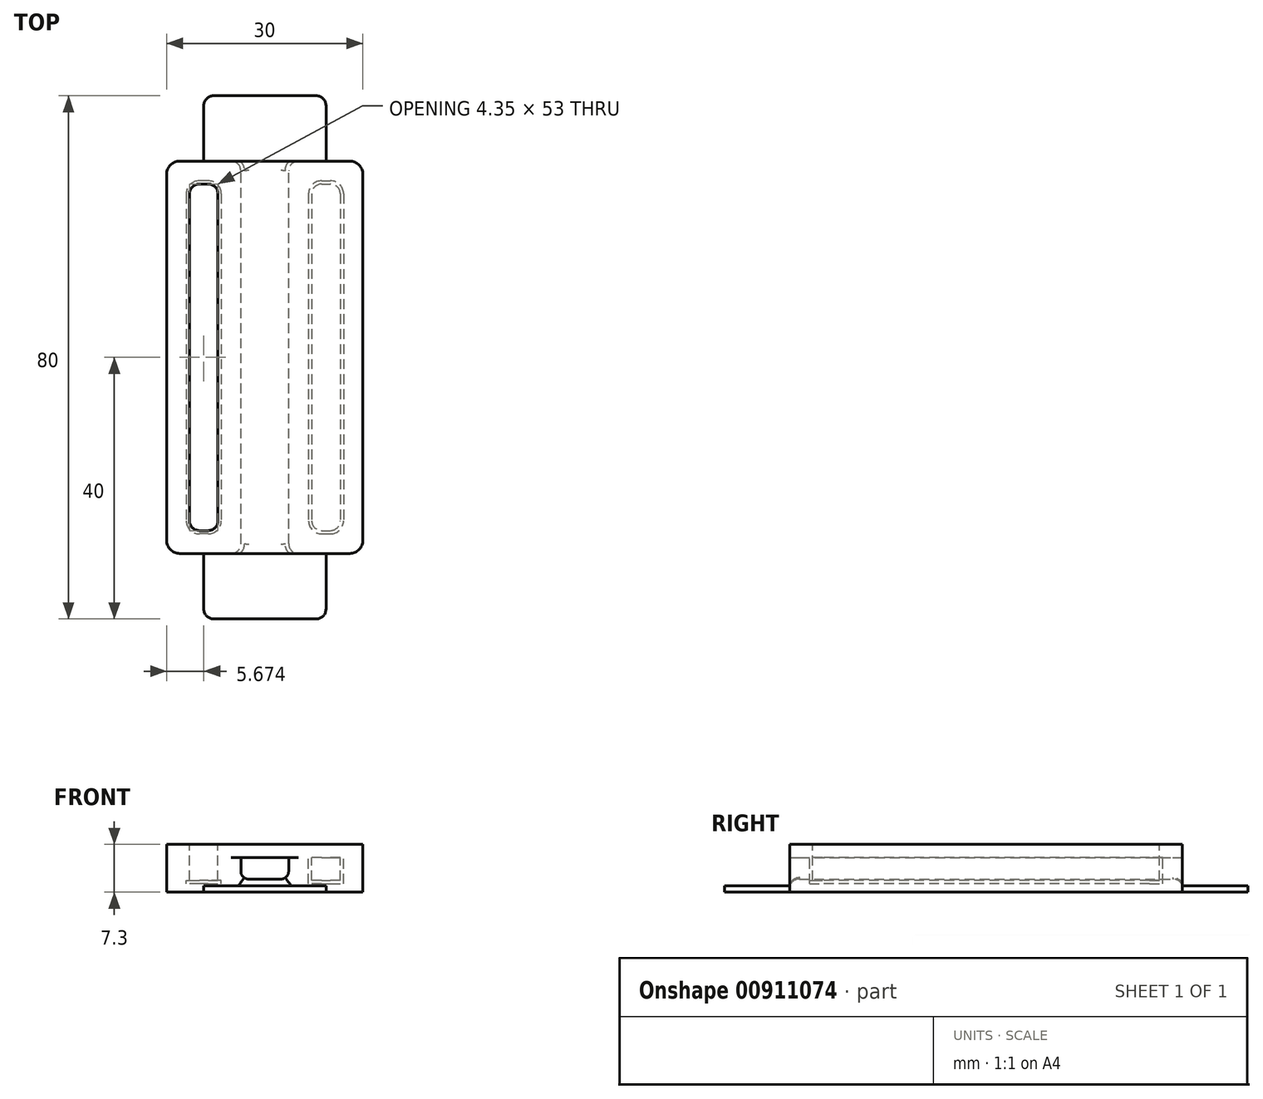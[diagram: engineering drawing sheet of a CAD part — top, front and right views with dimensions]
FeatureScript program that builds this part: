
annotation { "Feature Type Name" : "Feature", "Feature Type Description" : "" }
export const myFeature = defineFeature(function(context is Context, id is Id, definition is map)
    precondition{}
    {
        {
            var Q0;
            Q0=qCreatedBy(makeId("Front.planeOp"),FACE);
            var sketch = newSketch(context, id + "F0", { "sketchPlane" : qUnion([Q0])});
            skLineSegment(sketch, "E0", {"start": v(0, 0) * mm, "end": v(14.98, 0) * mm});
            skLineSegment(sketch, "E1", {"start": v(14.98, 0) * mm, "end": v(14.98, 5.3) * mm});
            skLineSegment(sketch, "E2", {"start": v(14.98, 5.3) * mm, "end": v(3.63, 5.3) * mm});
            skLineSegment(sketch, "E3", {"start": v(3.63, 5.3) * mm, "end": v(3.63, 3.2) * mm});
            skLineSegment(sketch, "E4", {"start": v(2.43, 2) * mm, "end": v(-0.25, 2) * mm});
            skLineSegment(sketch, "E5.MirrorCS", {"start": v(-15.02, 5.3) * mm, "end": v(-3.67, 5.3) * mm});
            skLineSegment(sketch, "E6.MirrorCS", {"start": v(-3.67, 5.3) * mm, "end": v(-3.67, 3.2) * mm});
            skLineSegment(sketch, "E7.MirrorCS", {"start": v(-2.47, 2) * mm, "end": v(0.2, 2) * mm});
            skLineSegment(sketch, "E8.MirrorCS", {"start": v(-15.02, 0) * mm, "end": v(-15.02, 5.3) * mm});
            skLineSegment(sketch, "E9.MirrorCS", {"start": v(0, 0) * mm, "end": v(-15.02, 0) * mm});
            skPoint(sketch, "E10.visualSharp", {"position": v(-3.67, 2) * mm});
            skArc(sketch, "E10.filletArc", {"start": v(-3.67, 3.2) * mm, "mid": v(-3.32, 2.35) * mm, "end": v(-2.47, 2) * mm});
            skPoint(sketch, "E11.visualSharp", {"position": v(3.63, 2) * mm});
            skArc(sketch, "E11.filletArc", {"start": v(2.43, 2) * mm, "mid": v(3.28, 2.35) * mm, "end": v(3.63, 3.2) * mm});
            skSolve(sketch);
        }
        {
            var Q0;
            Q0 = qSketchRegion(id + "F0", true);
            extrude(context, id + "F1", {"entities" : qUnion([Q0]), "depth" : 60 * mm, "offsetDistance" : 25 * mm});
        }
        {
            var Q0;
            Q0=makeQuery(id+"F1.opExtrude","SWEPT_FACE",FACE,{"disambiguationData":[OSD([sQuery(id+"F0.wireOp",EDGE,"E5.MirrorCS")])]});
            var sketch = newSketch(context, id + "F2", { "sketchPlane" : qUnion([Q0])});
            skLineSegment(sketch, "E12.bottom", {"start": v(-6.67, -3) * mm, "end": v(-12.02, -3) * mm});
            skLineSegment(sketch, "E12.top", {"start": v(-6.67, -57) * mm, "end": v(-12.02, -57) * mm});
            skLineSegment(sketch, "E12.left", {"start": v(-6.67, -3) * mm, "end": v(-6.67, -57) * mm});
            skLineSegment(sketch, "E12.right", {"start": v(-12.02, -3) * mm, "end": v(-12.02, -57) * mm});
            skLineSegment(sketch, "E13.MirrorCS", {"start": v(6.67, -3) * mm, "end": v(12.02, -3) * mm});
            skLineSegment(sketch, "E14.MirrorCS", {"start": v(12.02, -3) * mm, "end": v(12.02, -57) * mm});
            skLineSegment(sketch, "E15.MirrorCS", {"start": v(6.67, -57) * mm, "end": v(12.02, -57) * mm});
            skLineSegment(sketch, "E16.MirrorCS", {"start": v(6.67, -3) * mm, "end": v(6.67, -57) * mm});
            skSolve(sketch);
        }
        {
            var Q0;
            Q0 = qSketchRegion(id + "F2", true);
            extrude(context, id + "F3", {"entities" : qUnion([Q0]), "operationType" : NewBodyOperationType.REMOVE, "oppositeDirection" : true, "depth" : 4 * mm, "offsetDistance" : 25 * mm});
        }
        {
            var Q0;
            Q0=makeQuery(id+"F3.boolean.opBoolean","COPY",EDGE,{"derivedFrom":makeQuery(id+"F3.opExtrude","SWEPT_EDGE",EDGE,{"disambiguationData":[OSD([sQuery(id+"F2.wireOp",EDGE,"E12.bottom"),sQuery(id+"F2.wireOp",EDGE,"E12.left")])]})});
            var Q1;
            Q1=makeQuery(id+"F3.boolean.opBoolean","COPY",EDGE,{"derivedFrom":makeQuery(id+"F3.opExtrude","SWEPT_EDGE",EDGE,{"disambiguationData":[OSD([sQuery(id+"F2.wireOp",EDGE,"E12.bottom"),sQuery(id+"F2.wireOp",EDGE,"E12.right")])]})});
            var Q2;
            Q2=makeQuery(id+"F3.boolean.opBoolean","COPY",EDGE,{"derivedFrom":makeQuery(id+"F3.opExtrude","SWEPT_EDGE",EDGE,{"disambiguationData":[OSD([sQuery(id+"F2.wireOp",EDGE,"E12.top"),sQuery(id+"F2.wireOp",EDGE,"E12.right")])]})});
            var Q3;
            Q3=makeQuery(id+"F3.boolean.opBoolean","COPY",EDGE,{"derivedFrom":makeQuery(id+"F3.opExtrude","SWEPT_EDGE",EDGE,{"disambiguationData":[OSD([sQuery(id+"F2.wireOp",EDGE,"E12.top"),sQuery(id+"F2.wireOp",EDGE,"E12.left")])]})});
            var Q4;
            Q4=makeQuery(id+"F3.boolean.opBoolean","COPY",EDGE,{"derivedFrom":makeQuery(id+"F3.opExtrude","SWEPT_EDGE",EDGE,{"disambiguationData":[OSD([sQuery(id+"F2.wireOp",EDGE,"E13.MirrorCS"),sQuery(id+"F2.wireOp",EDGE,"E16.MirrorCS")])]})});
            var Q5;
            Q5=makeQuery(id+"F3.boolean.opBoolean","COPY",EDGE,{"derivedFrom":makeQuery(id+"F3.opExtrude","SWEPT_EDGE",EDGE,{"disambiguationData":[OSD([sQuery(id+"F2.wireOp",EDGE,"E13.MirrorCS"),sQuery(id+"F2.wireOp",EDGE,"E14.MirrorCS")])]})});
            var Q6;
            Q6=makeQuery(id+"F3.boolean.opBoolean","COPY",EDGE,{"derivedFrom":makeQuery(id+"F3.opExtrude","SWEPT_EDGE",EDGE,{"disambiguationData":[OSD([sQuery(id+"F2.wireOp",EDGE,"E15.MirrorCS"),sQuery(id+"F2.wireOp",EDGE,"E16.MirrorCS")])]})});
            var Q7;
            Q7=makeQuery(id+"F3.boolean.opBoolean","COPY",EDGE,{"derivedFrom":makeQuery(id+"F3.opExtrude","SWEPT_EDGE",EDGE,{"disambiguationData":[OSD([sQuery(id+"F2.wireOp",EDGE,"E14.MirrorCS"),sQuery(id+"F2.wireOp",EDGE,"E15.MirrorCS")])]})});
            var Q8;
            Q8=makeQuery(id+"F1.opExtrude","CAP_EDGE",EDGE,{"disambiguationData":[OSD([sQuery(id+"F0.wireOp",EDGE,"E8.MirrorCS")])],"isStart":true});
            var Q9;
            Q9=makeQuery(id+"F1.opExtrude","CAP_EDGE",EDGE,{"disambiguationData":[OSD([sQuery(id+"F0.wireOp",EDGE,"E1")])],"isStart":true});
            var Q10;
            Q10=makeQuery(id+"F1.opExtrude","CAP_EDGE",EDGE,{"disambiguationData":[OSD([sQuery(id+"F0.wireOp",EDGE,"E1")])],"isStart":false});
            var Q11;
            Q11=makeQuery(id+"F1.opExtrude","CAP_EDGE",EDGE,{"disambiguationData":[OSD([sQuery(id+"F0.wireOp",EDGE,"E8.MirrorCS")])],"isStart":false});
            fillet(context, id + "F4", {"entities" : qUnion([Q0, Q1, Q2, Q3, Q4, Q5, Q6, Q7, Q8, Q9, Q10, Q11]), "radius" : 2 * mm, "tangentPropagation" : true, "allowEdgeOverflow" : false});
        }
        {
            var Q0;
            Q0=qCreatedBy(makeId("Top.planeOp"),FACE);
            var sketch = newSketch(context, id + "F5", { "sketchPlane" : qUnion([Q0])});
            skLineSegment(sketch, "E17.bottom", {"start": v(9.35, 0) * mm, "end": v(-9.35, 0) * mm});
            skLineSegment(sketch, "E17.top", {"start": v(9.35, 10) * mm, "end": v(-9.35, 10) * mm});
            skLineSegment(sketch, "E17.left", {"start": v(9.35, 0) * mm, "end": v(9.35, 10) * mm});
            skLineSegment(sketch, "E17.right", {"start": v(-9.35, 0) * mm, "end": v(-9.35, 10) * mm});
            skPoint(sketch, "E18.0", {"position": v(9.35, -3) * mm});
            skPoint(sketch, "E19.0", {"position": v(-9.35, -3) * mm});
            skPoint(sketch, "E20.0", {"position": v(6.67, -30) * mm});
            skPoint(sketch, "E20.1", {"position": v(-6.67, -30) * mm});
            skLineSegment(sketch, "E21", {"start": v(6.67, -30) * mm, "end": v(-6.67, -30) * mm});
            skLineSegment(sketch, "E22.MirrorCS", {"start": v(9.35, -60) * mm, "end": v(9.35, -70) * mm});
            skLineSegment(sketch, "E23.MirrorCS", {"start": v(9.35, -70) * mm, "end": v(-9.35, -70) * mm});
            skLineSegment(sketch, "E24.MirrorCS", {"start": v(-9.35, -60) * mm, "end": v(-9.35, -70) * mm});
            skLineSegment(sketch, "E25.MirrorCS", {"start": v(9.35, -60) * mm, "end": v(-9.35, -60) * mm});
            skSolve(sketch);
        }
        {
            var Q0;
            Q0=makeQuery(id+"F5.imprint","IMPRINT",FACE,{"disambiguationData":[TD([[makeQuery(id+"F5.imprint","IMPRINT",EDGE,{"derivedFrom":sQuery(id+"F5.wireOp",EDGE,"E17.bottom")}),-1.0]])]});
            var Q1;
            Q1=makeQuery(id+"F5.imprint","IMPRINT",FACE,{"disambiguationData":[TD([[makeQuery(id+"F5.imprint","IMPRINT",EDGE,{"derivedFrom":sQuery(id+"F5.wireOp",EDGE,"E22.MirrorCS")}),-1.0]])]});
            extrude(context, id + "F6", {"entities" : qUnion([Q0, Q1]), "operationType" : NewBodyOperationType.ADD, "depth" : 1 * mm, "offsetDistance" : 25 * mm});
        }
        {
            var Q0;
            Q0=makeQuery(id+"F6.opExtrude","SWEPT_EDGE",EDGE,{"disambiguationData":[OSD([sQuery(id+"F5.wireOp",EDGE,"E23.MirrorCS"),sQuery(id+"F5.wireOp",EDGE,"E24.MirrorCS")])]});
            var Q1;
            Q1=makeQuery(id+"F6.opExtrude","SWEPT_EDGE",EDGE,{"disambiguationData":[OSD([sQuery(id+"F5.wireOp",EDGE,"E22.MirrorCS"),sQuery(id+"F5.wireOp",EDGE,"E23.MirrorCS")])]});
            var Q2;
            Q2=makeQuery(id+"F1.opExtrude","CAP_EDGE",EDGE,{"disambiguationData":[OSD([sQuery(id+"F0.wireOp",EDGE,"E4"),sQuery(id+"F0.wireOp",EDGE,"E7.MirrorCS")])],"isStart":false});
            var Q3;
            Q3=makeQuery(id+"F1.opExtrude","CAP_EDGE",EDGE,{"disambiguationData":[OSD([sQuery(id+"F0.wireOp",EDGE,"E4"),sQuery(id+"F0.wireOp",EDGE,"E7.MirrorCS")])],"isStart":true});
            var Q4;
            Q4=makeQuery(id+"F6.opExtrude","SWEPT_EDGE",EDGE,{"disambiguationData":[OSD([sQuery(id+"F5.wireOp",EDGE,"E17.top"),sQuery(id+"F5.wireOp",EDGE,"E17.right")])]});
            var Q5;
            Q5=makeQuery(id+"F6.opExtrude","SWEPT_EDGE",EDGE,{"disambiguationData":[OSD([sQuery(id+"F5.wireOp",EDGE,"E17.top"),sQuery(id+"F5.wireOp",EDGE,"E17.left")])]});
            fillet(context, id + "F7", {"entities" : qUnion([Q0, Q1, Q2, Q3, Q4, Q5]), "radius" : 1.5 * mm, "tangentPropagation" : true, "allowEdgeOverflow" : false});
        }
        {
            var Q0;
            Q0=makeQuery(id+"F1.opExtrude","SWEPT_FACE",FACE,{"disambiguationData":[OSD([sQuery(id+"F0.wireOp",EDGE,"E5.MirrorCS")])]});
            var sketch = newSketch(context, id + "F8", { "sketchPlane" : qUnion([Q0])});
            skLineSegment(sketch, "E26.0", {"start": v(-12.02, -5) * mm, "end": v(-12.02, -55) * mm});
            skArc(sketch, "E26.1", {"start": v(-10.02, -57) * mm, "mid": v(-11.44, -56.41) * mm, "end": v(-12.02, -55) * mm});
            skLineSegment(sketch, "E26.2", {"start": v(-8.67, -57) * mm, "end": v(-10.02, -57) * mm});
            skArc(sketch, "E26.3", {"start": v(-6.67, -55) * mm, "mid": v(-7.26, -56.41) * mm, "end": v(-8.67, -57) * mm});
            skLineSegment(sketch, "E26.4", {"start": v(-6.67, -5) * mm, "end": v(-6.67, -55) * mm});
            skArc(sketch, "E26.5", {"start": v(-8.67, -3) * mm, "mid": v(-7.26, -3.59) * mm, "end": v(-6.67, -5) * mm});
            skLineSegment(sketch, "E26.6", {"start": v(-8.67, -3) * mm, "end": v(-10.02, -3) * mm});
            skArc(sketch, "E26.7", {"start": v(-12.02, -5) * mm, "mid": v(-11.44, -3.59) * mm, "end": v(-10.02, -3) * mm});
            skArc(sketch, "E27.0", {"start": v(-8.67, -3.5) * mm, "mid": v(-7.61, -3.94) * mm, "end": v(-7.17, -5) * mm});
            skLineSegment(sketch, "E27.1", {"start": v(-8.67, -3.5) * mm, "end": v(-10.02, -3.5) * mm});
            skLineSegment(sketch, "E27.2", {"start": v(-7.17, -5) * mm, "end": v(-7.17, -55) * mm});
            skArc(sketch, "E27.3", {"start": v(-11.52, -5) * mm, "mid": v(-11.08, -3.94) * mm, "end": v(-10.02, -3.5) * mm});
            skArc(sketch, "E27.4", {"start": v(-7.17, -55) * mm, "mid": v(-7.61, -56.06) * mm, "end": v(-8.67, -56.5) * mm});
            skLineSegment(sketch, "E27.5", {"start": v(-8.67, -56.5) * mm, "end": v(-10.02, -56.5) * mm});
            skArc(sketch, "E27.6", {"start": v(-10.02, -56.5) * mm, "mid": v(-11.08, -56.06) * mm, "end": v(-11.52, -55) * mm});
            skLineSegment(sketch, "E27.7", {"start": v(-11.52, -5) * mm, "end": v(-11.52, -55) * mm});
            skLineSegment(sketch, "E28.MirrorCS", {"start": v(11.52, -5) * mm, "end": v(11.52, -55) * mm});
            skArc(sketch, "E29.MirrorCS", {"start": v(10.02, -56.5) * mm, "mid": v(11.08, -56.06) * mm, "end": v(11.52, -55) * mm});
            skLineSegment(sketch, "E30.MirrorCS", {"start": v(8.67, -56.5) * mm, "end": v(10.02, -56.5) * mm});
            skArc(sketch, "E31.MirrorCS", {"start": v(7.17, -55) * mm, "mid": v(7.61, -56.06) * mm, "end": v(8.67, -56.5) * mm});
            skLineSegment(sketch, "E32.MirrorCS", {"start": v(7.17, -5) * mm, "end": v(7.17, -55) * mm});
            skArc(sketch, "E33.MirrorCS", {"start": v(8.67, -3.5) * mm, "mid": v(7.61, -3.94) * mm, "end": v(7.17, -5) * mm});
            skLineSegment(sketch, "E34.MirrorCS", {"start": v(8.67, -3.5) * mm, "end": v(10.02, -3.5) * mm});
            skArc(sketch, "E35.MirrorCS", {"start": v(11.52, -5) * mm, "mid": v(11.08, -3.94) * mm, "end": v(10.02, -3.5) * mm});
            skLineSegment(sketch, "E36.0", {"start": v(-15.02, -58) * mm, "end": v(-15.02, -2) * mm});
            skArc(sketch, "E36.1", {"start": v(-15.02, -58) * mm, "mid": v(-14.44, -59.41) * mm, "end": v(-13.02, -60) * mm});
            skLineSegment(sketch, "E36.2", {"start": v(-13.02, -60) * mm, "end": v(-5.17, -60) * mm});
            skLineSegment(sketch, "E36.3", {"start": v(12.98, -60) * mm, "end": v(5.13, -60) * mm});
            skArc(sketch, "E36.4", {"start": v(12.98, -60) * mm, "mid": v(14.4, -59.41) * mm, "end": v(14.98, -58) * mm});
            skLineSegment(sketch, "E36.5", {"start": v(14.98, -58) * mm, "end": v(14.98, -2) * mm});
            skArc(sketch, "E36.6", {"start": v(14.98, -2) * mm, "mid": v(14.4, -0.59) * mm, "end": v(12.98, 0) * mm});
            skLineSegment(sketch, "E36.7", {"start": v(12.98, 0) * mm, "end": v(5.13, 0) * mm});
            skLineSegment(sketch, "E36.8", {"start": v(-13.02, 0) * mm, "end": v(-5.17, 0) * mm});
            skArc(sketch, "E36.9", {"start": v(-13.02, 0) * mm, "mid": v(-14.44, -0.59) * mm, "end": v(-15.02, -2) * mm});
            skLineSegment(sketch, "E37", {"start": v(5.13, -60) * mm, "end": v(-5.17, -60) * mm});
            skLineSegment(sketch, "E38", {"start": v(5.13, 0) * mm, "end": v(-5.17, 0) * mm});
            skSolve(sketch);
        }
        {
            var Q0;
            Q0=makeQuery(id+"F8.imprint","IMPRINT",FACE,{"disambiguationData":[TD([[makeQuery(id+"F8.imprint","IMPRINT",EDGE,{"derivedFrom":sQuery(id+"F8.wireOp",EDGE,"E28.MirrorCS")}),-1.0]])]});
            var Q1;
            Q1=makeQuery(id+"F8.imprint","IMPRINT",FACE,{"disambiguationData":[TD([[makeQuery(id+"F8.imprint","IMPRINT",EDGE,{"derivedFrom":sQuery(id+"F8.wireOp",EDGE,"E27.0")}),-1.0]])]});
            extrude(context, id + "F9", {"entities" : qUnion([Q0, Q1]), "oppositeDirection" : true, "depth" : 3.5 * mm, "offsetDistance" : 25 * mm, "hasSecondDirection" : true, "secondDirectionOppositeDirection" : false, "secondDirectionDepth" : 2 * mm});
        }
        {
            var Q0;
            Q0=makeQuery(id+"F8.imprint","IMPRINT",FACE,{"disambiguationData":[TD([[makeQuery(id+"F8.imprint","IMPRINT",EDGE,{"derivedFrom":sQuery(id+"F8.wireOp",EDGE,"E26.0")}),-1.0]])]});
            var Q1;
            Q1=makeQuery(id+"F8.imprint","IMPRINT",FACE,{"disambiguationData":[TD([[makeQuery(id+"F8.imprint","IMPRINT",EDGE,{"derivedFrom":sQuery(id+"F8.wireOp",EDGE,"E28.MirrorCS")}),1.0]])]});
            var Q2;
            Q2=makeQuery(id+"F8.imprint","IMPRINT",FACE,{"disambiguationData":[TD([[makeQuery(id+"F8.imprint","IMPRINT",EDGE,{"derivedFrom":sQuery(id+"F8.wireOp",EDGE,"E26.0")}),1.0]])]});
            extrude(context, id + "F10", {"entities" : qUnion([Q0, Q1, Q2]), "operationType" : NewBodyOperationType.ADD, "depth" : 2 * mm, "offsetDistance" : 25 * mm});
        }
    });
